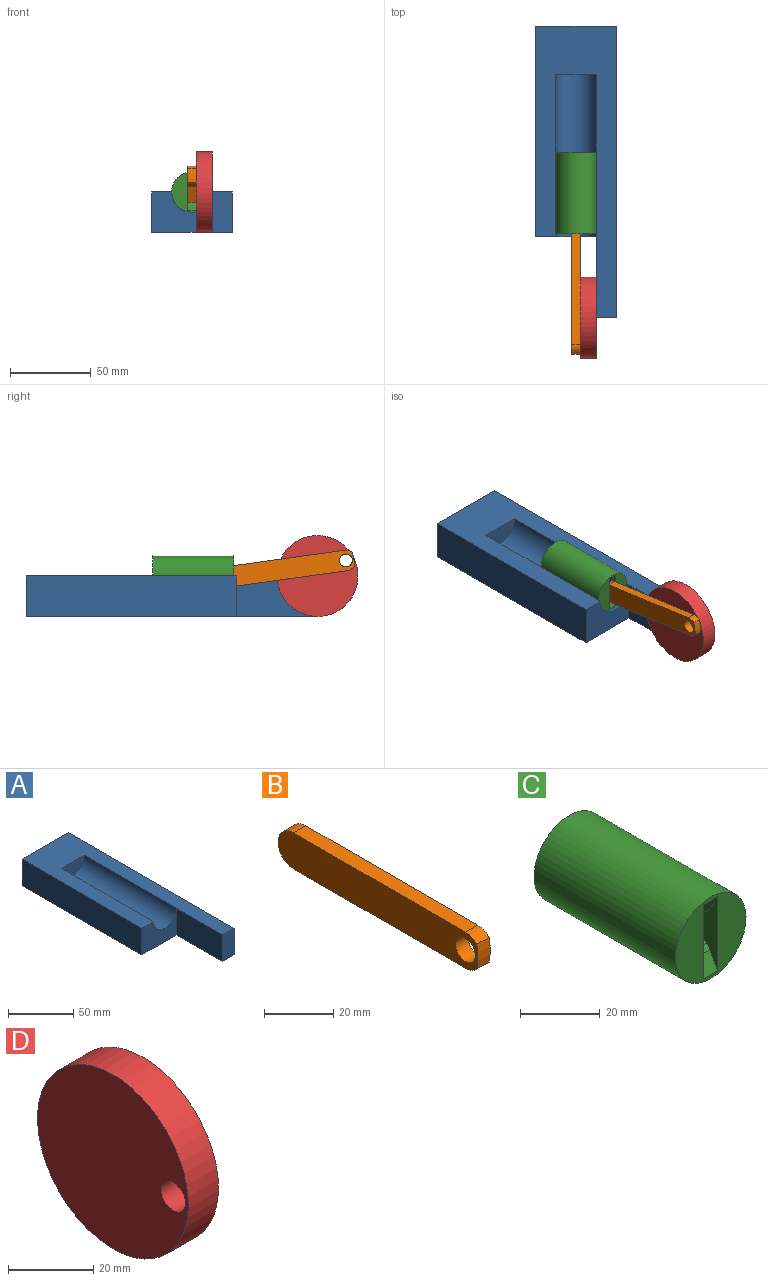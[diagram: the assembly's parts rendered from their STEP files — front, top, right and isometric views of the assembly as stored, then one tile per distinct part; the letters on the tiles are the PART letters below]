
ASSEMBLY  parts=4 mates=4
PART A: 10 faces, bbox 50x180x25 mm
  f0: plane 180x25mm, normal (1,0,0), area 4500mm2, adj f1,f4,f5,f9
  f1: plane 50x25mm, normal (0,1,0), area 1250mm2, adj f0,f2,f4,f5
  f2: plane 130x25mm, normal (-1,0,0), area 3250mm2, adj f1,f3,f4,f5
  f3: plane 37.5x25mm, normal (0,-1,0), area 692.1mm2, adj f2,f4,f5,f6,f8
  f4: plane 180x50mm, normal (0,0,1), area 4625mm2, adj f0,f1,f2,f3,f6,f7,f8,f9
  f5: plane 180x50mm, normal (0,0,-1), area 7125mm2, adj f0,f1,f2,f3,f8,f9
  f6: cylinder r=12.5mm len=100mm, axis (0,-1,0), area 3927mm2, adj f3,f4,f7
  f7: plane 25x12.5mm, normal (0,-1,0), area 245.4mm2, adj f4,f6
  f8: plane 50x25mm, normal (-1,0,0), area 1250mm2, adj f3,f4,f5,f9
  f9: plane 25x12.5mm, normal (0,-1,0), area 312.5mm2, adj f0,f4,f5,f8
PART B: 9 faces, bbox 5x81.4x12.7 mm
  f0: plane 70x5mm, normal (0,0,1), area 350mm2, adj f1,f5,f7,f8
  f1: cylinder r=6.35mm len=12.7mm, axis (1,0,0), area 99.7mm2, adj f0,f2,f7,f8
  f2: plane 70x5mm, normal (0,0,-1), area 350mm2, adj f1,f3,f7,f8
  f3: cylinder r=6.35mm len=5mm, axis (1,0,0), area 25.8mm2, adj f2,f4,f7,f8
  f4: cylinder r=25mm len=8.72mm, axis (1,0,0), area 43.8mm2, adj f3,f5,f7,f8
  f5: cylinder r=6.35mm len=5mm, axis (1,0,0), area 25.8mm2, adj f0,f4,f7,f8
  f6: cylinder r=4mm len=8mm, axis (1,0,0), area 125.7mm2, adj f7,f8
  f7: plane 81.35x12.7mm, normal (-1,0,0), area 957.3mm2, adj f0,f1,f2,f3,f4,f5,f6
  f8: plane 81.35x12.7mm, normal (1,0,0), area 957.3mm2, adj f0,f1,f2,f3,f4,f5,f6
PART C: 10 faces, bbox 25x50x25 mm
  f0: cylinder r=12.5mm len=50mm, axis (0,-1,0), area 3927mm2, adj f1,f2
  f1: plane 25x25mm, normal (0,1,0), area 490.9mm2, adj f0
  f2: plane 25x25mm, normal (0,-1,0), area 377.2mm2, adj f0,f4,f5,f6,f7
  f3: cylinder r=6.35mm len=9.86mm, axis (1,0,0), area 56.4mm2, adj f4,f5,f8,f9
  f4: plane 22.74x6.35mm, normal (1,0,0), area 79.1mm2, adj f2,f3,f6,f7,f8,f9
  f5: plane 22.74x6.35mm, normal (-1,0,0), area 79.1mm2, adj f2,f3,f6,f7,f8,f9
  f6: plane 5x5mm, normal (0,-0.87,0.49), area 28.6mm2, adj f2,f4,f5,f8
  f7: plane 5x5mm, normal (0,-0.87,-0.49), area 28.6mm2, adj f2,f4,f5,f9
  f8: cylinder r=5mm len=5mm, axis (1,0,0), area 9.5mm2, adj f3,f4,f5,f6
  f9: cylinder r=5mm len=5mm, axis (1,0,0), area 9.5mm2, adj f3,f4,f5,f7
PART D: 4 faces, bbox 10x50x50 mm
  f0: cylinder r=25mm len=50mm, axis (1,0,0), area 1570.8mm2, adj f2,f3
  f1: cylinder r=4mm len=10mm, axis (1,0,0), area 251.3mm2, adj f2,f3
  f2: plane 50x50mm, normal (-1,0,0), area 1913.2mm2, adj f0,f1
  f3: plane 50x50mm, normal (1,0,0), area 1913.2mm2, adj f0,f1
PLACE A t=(-0.53,-166.98,29.69)mm fixed
PLACE B rot(axis=(-1,0,0),7.9deg) t=(-0.53,-169.23,21.02)mm
PLACE C t=(-0.53,-165.19,29.69)mm
PLACE D rot(axis=(-1,0,0),28.7deg) t=(-0.53,-193.06,-22.4)mm
MATE slider C.f0 <-> A.f6  axis (0,-1,0) through (-0.53,-230.19,54.69)mm
MATE ball B.f1 <-> C.f3  axis (1,0,0) through (-0.53,-230.19,54.69)mm
MATE revolute D.f0 <-> A.f8  axis (1,0,0) through (11.97,-281.98,54.69)mm
MATE revolute B.f3 <-> D.f1  axis (1,0,0) through (1.97,-299.53,64.28)mm
